# Revit family: Haworth_PoppyLounge_Chair
name_source: partatom
category: Furniture
revit_build: Autodesk Revit 2018 (Build: 20170223_1515(x64)
units: mm (PartAtom-declared; Revit-internal decimal feet)

## family parameters
Always vertical = Yes
Cut with Voids When Loaded = No
OmniClass Number = 23.40.70.14.64.11
OmniClass Title = Office Furniture
Room Calculation Point = No
Shared = No
Work Plane-Based = No

## types (2) — shared parameters
Actual Depth = 29.5 "
Actual Height = 32.75 "
Actual Width = 31 "
Assembly Code = E2020200
Description = Haworth Poppy Lounge Chair
Manufacturer = Haworth
Model = SLP
Product URL = https://www.haworth.com
Revision Number = 1
Sustainability Info = https://www.haworth.com
URL = http://www.haworth.com
Warranty = http://www.haworth.com

## per-type parameters (varying)
| type | Metal Base | Wood Base |
| SLP-xx-S - Wood Base | No | Yes |
| SLP-xx-T - Metal Base | Yes | No |

## geometry (parser evidence)
native form markers: Sweep x10
no freeform markers — native parametric forms only
